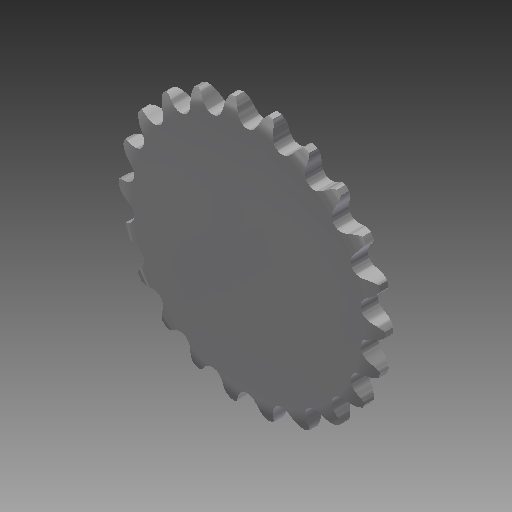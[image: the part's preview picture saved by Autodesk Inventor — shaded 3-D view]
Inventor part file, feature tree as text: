
AUTODESK INVENTOR PART (.ipt)
format: ipt  version: 2017 (Build 210142000, 142)  size: 613,888 bytes
history: native  units: mm
features: other x6, extrude x2, pattern_linear x1, pattern_circular x1
ambient origin geometry x8: Origin, YZ Plane, XZ Plane, XY Plane, X Axis, Y Axis, Z Axis, Center Point
bodies: Solid1 (feature_tree)
feature tree (10):
  other  "Theoretical Tooth Profile"
  other  "Tooth Profile"
  other  "Section Profile"
  other  "Shroud"
  other  "Strand"
  pattern_linear  "Strand Pattern"  Spacing1=44.619381mm  [1 undecoded]
  extrude  "Theoretical Tooth"  Depth=2.855993mm
  extrude  "Tooth"  Depth=1.697355mm
  pattern_circular  "Tooth Pattern"  [2 undecoded]
  other  "Timing Plane"
note: 3 required parameter values undecoded (feature->parameter linkage not recoverable at this tier; creation-order binding heuristic only, values carry confidence <= 0.55)
